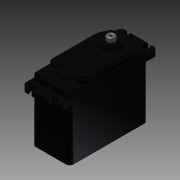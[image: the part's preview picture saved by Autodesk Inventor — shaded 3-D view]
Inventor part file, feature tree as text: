
AUTODESK INVENTOR PART (.ipt)
format: ipt  version: 2014 SP2 (Build 180246200, 246)  size: 424,960 bytes
history: native  units: in
note: dims shown in document units (in); Inventor stores cm internally (conversion verified against a paired STEP export)
features: extrude x17, sketch x16, projected_geometry x3, fillet x2, plane x1, chamfer x1
ambient origin geometry x8: Origin, YZ Plane, XZ Plane, XY Plane, X Axis, Y Axis, Z Axis, Center Point
bodies: Solid1 (feature_tree)
feature tree (40):
  extrude  "Extrusion1"  Depth=1.832in
  extrude  "Extrusion2"  Depth=1.04in
  extrude  "Extrusion3"  Depth=0.04in TaperAngle=0.0deg
  extrude  "Extrusion4"  Depth=0.449in
  extrude  "Extrusion5"  Depth=0.0835in
  fillet  "Fillet1"  Radius=0.0835in
  plane  "Work Plane1"
  extrude  "Extrusion6"  Depth=0.9645in
  fillet  "Fillet2"  Radius=0.0175in
  extrude  "Extrusion7"  [1 undecoded]
  extrude  "Extrusion8"  Depth=2.907in
  extrude  "Extrusion9"  Depth=0.125in
  extrude  "Extrusion10"  Depth=0.149in
  extrude  "Extrusion11"  Depth=0.17in
  extrude  "Extrusion12"  Depth=0.1575in TaperAngle=0.0deg
  extrude  "Extrusion14"  Depth=0.1035in
  extrude  "Extrusion15"  Depth=0.08in
  extrude  "Extrusion16"  Depth=0.0645in TaperAngle=0.0deg
  extrude  "Extrusion17"  Depth=0.077in TaperAngle=0.0deg
  chamfer  "Chamfer1"  Distance=0.43in
  extrude  "Extrusion18"  Depth=0.025in TaperAngle=0.0deg
  sketch  "Sketch1"  dims[d0=2.309in d1=1.832in]
  sketch  "Sketch2"  dims[d2=1.121in d3=0.0in d4=1.04in]
  sketch  "Sketch3"  dims[d5=2.2635in d7=0.04in d8=0.0in]
  projected_geometry  "Projected Loop1"
  sketch  "Sketch4"  dims[d9=0.026in d10=0.449in]
  sketch  "Sketch5"  dims[d12=0.488in d13=0.189in d14=0.0835in d15=0.0in]
  sketch  "Sketch6"  dims[d16=0.044in d17=0.0in d18=0.9645in d19=0.0175in d20=0.0in]
  projected_geometry  "Projected Loop2"
  sketch  "Sketch7"  dims[d21=0.125in d22=-0.103in]
  sketch  "Sketch8"  dims[d23=1.0915in d24=2.907in]
  sketch  "Sketch9"  dims[d25=0.1575in d26=0.0in d27=0.125in]
  sketch  "Sketch10"  dims[d28=0.149in d29=0.149in]
  sketch  "Sketch11"  dims[d30=0.1995in d31=0.17in]
  sketch  "Sketch12"  dims[d32=0.17in d33=0.1575in d34=0.0in]
  sketch  "Sketch14"  dims[d35=0.184in d36=0.1035in]
  sketch  "Sketch15"  dims[d37=0.1575in d38=0.0in d39=0.08in]
  sketch  "Sketch16"  dims[d40=0.1345in d41=0.0645in d42=0.0in]
  projected_geometry  "Projected Loop3"
  sketch  "Sketch17"  dims[d43=0.5455in d44=0.077in d45=0.0in d46=0.43in d47=0.025in d48=0.0in d49=0.225in d50=0.127in d51=0.0in d58=1.0in d59=0.0in d60=1.0in d61=0.0in d62=1.0in d63=0.0in d64=1.0in d65=0.0in d66=0.023in d67=0.125in d68=45.0deg d70=0.1in d72=0.0886in d73=0.1772in d74=0.0591in d75=0.0591in d76=1.1811in d78=0.0591in d79=0.3937in d81=1.0in d83=0.3in d84=0.0in]
note: 1 required parameter value undecoded (feature->parameter linkage not recoverable at this tier; creation-order binding heuristic only, values carry confidence <= 0.55)
